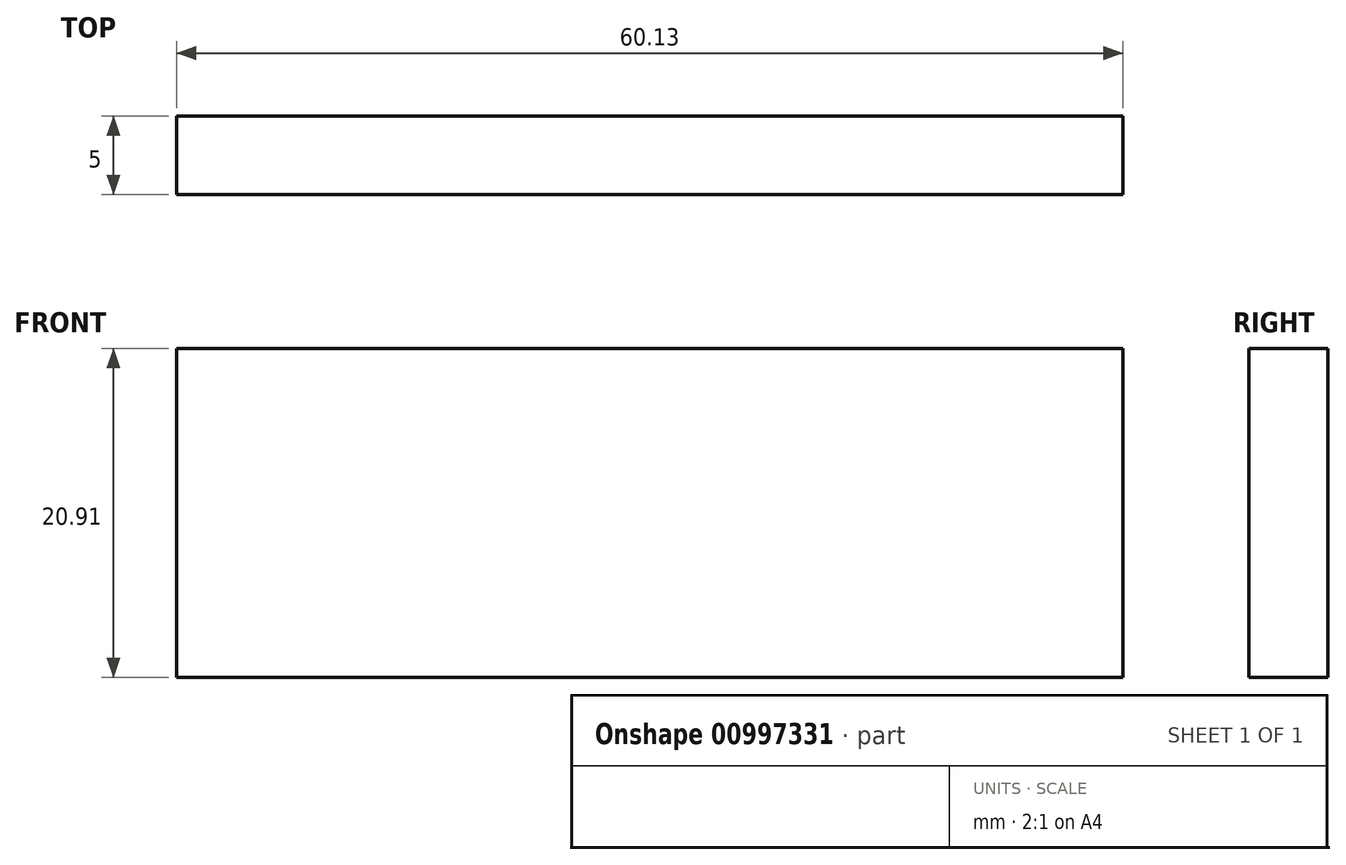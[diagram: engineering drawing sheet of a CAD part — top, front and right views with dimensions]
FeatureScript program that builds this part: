
annotation { "Feature Type Name" : "Feature", "Feature Type Description" : "" }
export const myFeature = defineFeature(function(context is Context, id is Id, definition is map)
    precondition{}
    {
        {
            var Q0;
            Q0=qCreatedBy(makeId("Front.planeOp"),FACE);
            var sketch = newSketch(context, id + "F0", { "sketchPlane" : qUnion([Q0])});
            skLineSegment(sketch, "E0.bottom", {"start": v(-52.68, 15.08) * mm, "end": v(7.45, 15.08) * mm});
            skLineSegment(sketch, "E0.top", {"start": v(-52.68, -5.83) * mm, "end": v(7.45, -5.83) * mm});
            skLineSegment(sketch, "E0.left", {"start": v(-52.68, 15.08) * mm, "end": v(-52.68, -5.83) * mm});
            skLineSegment(sketch, "E0.right", {"start": v(7.45, 15.08) * mm, "end": v(7.45, -5.83) * mm});
            skSolve(sketch);
        }
        {
            var Q0;
            Q0 = qSketchRegion(id + "F0", true);
            extrude(context, id + "F1", {"entities" : qUnion([Q0]), "depth" : 5 * mm, "offsetDistance" : 25 * mm});
        }
    });
